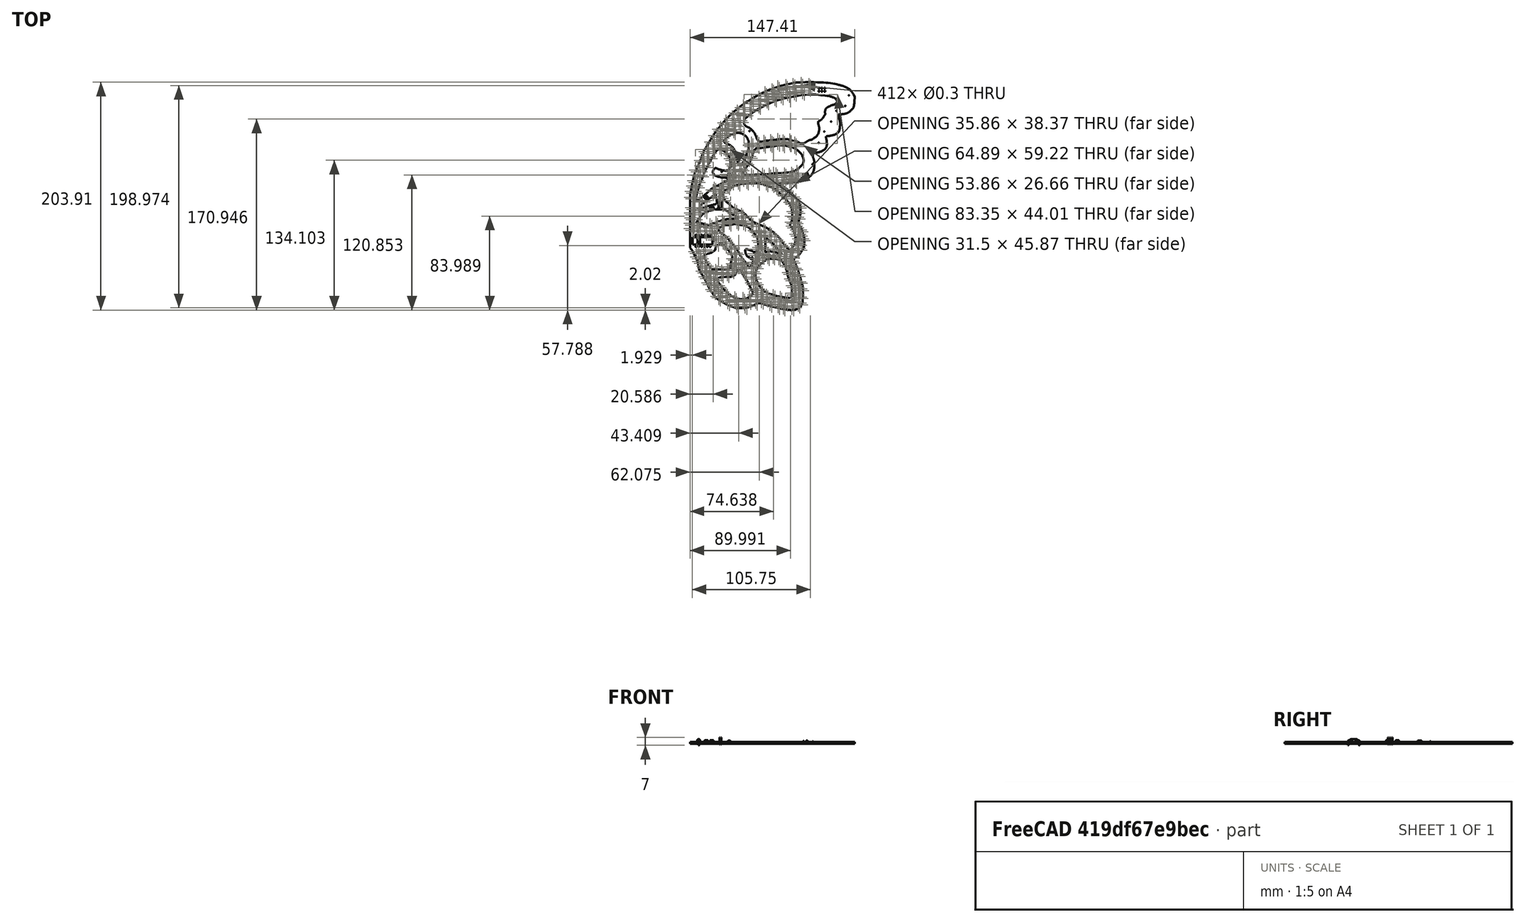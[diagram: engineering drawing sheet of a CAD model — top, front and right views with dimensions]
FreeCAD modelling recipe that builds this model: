
FCSTD DOCUMENT  (FreeCAD 0.21R30454 (Git))
Label: StarboardWing
License: All rights reserved
LicenseURL: http://en.wikipedia.org/wiki/All_rights_reserved
objects: App::Link×254, Part::Feature×9, App::Part×4, PartDesign::CoordinateSystem×1
note: 10 computed .brp shape members not serialized (recipe doc carries the construction recipe); baked Part::Feature solids carry a one-line shape summary decoded from their .brp

FEATURE [PartDesign::CoordinateSystem] Local_CS_1785
  AttacherType = Attacher::AttachEngine3D
  MapMode = 2
  Support = -> [X_Axis001]
FEATURE [Part::Feature] Pcb_1785
  shape: bbox 147.4 x 203.9 x 1.6 mm, 4422 faces (baked)
FEATURE [App::Part] Board_Geoms_1785
  Group = -> [Pcb_1785]
  Origin = -> Origin
FEATURE [Part::Feature] Shape  label="D136_LED_RGB_1210_62a520bec992"
  Placement = pos=(204.1,-82.7,0) rot=(0,0,1;0rad)
  shape: bbox 3.2 x 2.7 x 1.11 mm, 98 faces (baked)
FEATURE [App::Link] D136_LED_RGB_1210_62a520bec992_ln_  label="D150_LED_RGB_1210_12039ab7eeb1"
  LinkPlacement = pos=(181.3,-75,0) rot=(0,0,1;0rad)
  LinkedObject = -> Shape
  Placement = pos=(181.3,-75,0) rot=(0,0,1;0rad)
FEATURE [App::Link] D136_LED_RGB_1210_62a520bec992_ln_001  label="D23_LED_RGB_1210_ea9085552632"
  LinkPlacement = pos=(183.359,-164.826,0) rot=(0,0,1;0rad)
  LinkedObject = -> Shape
  Placement = pos=(183.359,-164.826,0) rot=(0,0,1;0rad)
FEATURE [App::Link] D136_LED_RGB_1210_62a520bec992_ln_002  label="D9_LED_RGB_1210_9001bbad8535"
  LinkPlacement = pos=(187.8,-129.2,0) rot=(0,0,1;0rad)
  LinkedObject = -> Shape
  Placement = pos=(187.8,-129.2,0) rot=(0,0,1;0rad)
FEATURE [App::Link] D136_LED_RGB_1210_62a520bec992_ln_003  label="D134_LED_RGB_1210_4c37d6cb8a8d"
  LinkPlacement = pos=(215.859,-120.026,0) rot=(0,0,1;0rad)
  LinkedObject = -> Shape
  Placement = pos=(215.859,-120.026,0) rot=(0,0,1;0rad)
FEATURE [App::Link] D136_LED_RGB_1210_62a520bec992_ln_004  label="D81_LED_RGB_1210_f8f1b236e2ee"
  LinkPlacement = pos=(224.9,-174.7,0) rot=(0,0,1;0rad)
  LinkedObject = -> Shape
  Placement = pos=(224.9,-174.7,0) rot=(0,0,1;0rad)
FEATURE [App::Link] D136_LED_RGB_1210_62a520bec992_ln_005  label="D7_LED_RGB_1210_8e7839006ea9"
  LinkPlacement = pos=(176.2,-132.6,0) rot=(0,0,1;0rad)
  LinkedObject = -> Shape
  Placement = pos=(176.2,-132.6,0) rot=(0,0,1;0rad)
FEATURE [App::Link] D136_LED_RGB_1210_62a520bec992_ln_006  label="D193_LED_RGB_1210_c832a5a088d9"
  LinkPlacement = pos=(307.759,-11.8264,0) rot=(0,0,1;0rad)
  LinkedObject = -> Shape
  Placement = pos=(307.759,-11.8264,0) rot=(0,0,1;0rad)
FEATURE [App::Link] D136_LED_RGB_1210_62a520bec992_ln_007  label="D158_LED_RGB_1210_09a3a09bfe6b"
  LinkPlacement = pos=(196.1,-51.9,0) rot=(0,0,1;0rad)
  LinkedObject = -> Shape
  Placement = pos=(196.1,-51.9,0) rot=(0,0,1;0rad)
FEATURE [App::Link] D136_LED_RGB_1210_62a520bec992_ln_008  label="D114_LED_RGB_1210_9c8997dbba9e"
  LinkPlacement = pos=(260.5,-102.9,0) rot=(0,0,1;0rad)
  LinkedObject = -> Shape
  Placement = pos=(260.5,-102.9,0) rot=(0,0,1;0rad)
FEATURE [App::Link] D136_LED_RGB_1210_62a520bec992_ln_009  label="D36_LED_RGB_1210_b757f64c7942"
  LinkPlacement = pos=(201.959,-191.026,0) rot=(0,0,1;0rad)
  LinkedObject = -> Shape
  Placement = pos=(201.959,-191.026,0) rot=(0,0,1;0rad)
FEATURE [App::Link] D136_LED_RGB_1210_62a520bec992_ln_010  label="D218_LED_RGB_1210_dde6179954a0"
  LinkPlacement = pos=(276.2,-62.7,0) rot=(0,0,1;0rad)
  LinkedObject = -> Shape
  Placement = pos=(276.2,-62.7,0) rot=(0,0,1;0rad)
FEATURE [App::Link] D136_LED_RGB_1210_62a520bec992_ln_011  label="D55_LED_RGB_1210_d54d391acb56"
  LinkPlacement = pos=(261.1,-194.9,0) rot=(0,0,1;0rad)
  LinkedObject = -> Shape
  Placement = pos=(261.1,-194.9,0) rot=(0,0,1;0rad)
FEATURE [App::Link] D136_LED_RGB_1210_62a520bec992_ln_012  label="D141_LED_RGB_1210_632e38c38ab6"
  LinkPlacement = pos=(208.9,-73.4,0) rot=(0,0,1;0rad)
  LinkedObject = -> Shape
  Placement = pos=(208.9,-73.4,0) rot=(0,0,1;0rad)
FEATURE [App::Link] D136_LED_RGB_1210_62a520bec992_ln_013  label="D222_LED_RGB_1210_c6c191f252d3"
  LinkPlacement = pos=(259.159,-53.4264,0) rot=(0,0,1;0rad)
  LinkedObject = -> Shape
  Placement = pos=(259.159,-53.4264,0) rot=(0,0,1;0rad)
FEATURE [App::Link] D136_LED_RGB_1210_62a520bec992_ln_014  label="D146_LED_RGB_1210_0157bd98a823"
  LinkPlacement = pos=(190.5,-58.9,0) rot=(0,0,1;0rad)
  LinkedObject = -> Shape
  Placement = pos=(190.5,-58.9,0) rot=(0,0,1;0rad)
FEATURE [App::Link] D136_LED_RGB_1210_62a520bec992_ln_015  label="D186_LED_RGB_1210_e3d56bbb0ae5"
  LinkPlacement = pos=(270.65,-7.45,0) rot=(0,0,1;0rad)
  LinkedObject = -> Shape
  Placement = pos=(270.65,-7.45,0) rot=(0,0,1;0rad)
FEATURE [App::Link] D136_LED_RGB_1210_62a520bec992_ln_016  label="D164_LED_RGB_1210_3ddcdd4b0932"
  LinkPlacement = pos=(209.2,-38.3,0) rot=(0,0,1;0rad)
  LinkedObject = -> Shape
  Placement = pos=(209.2,-38.3,0) rot=(0,0,1;0rad)
FEATURE [App::Link] D136_LED_RGB_1210_62a520bec992_ln_017  label="D64_LED_RGB_1210_adbd692ccdd2"
  LinkPlacement = pos=(259.759,-170.426,0) rot=(0,0,1;0rad)
  LinkedObject = -> Shape
  Placement = pos=(259.759,-170.426,0) rot=(0,0,1;0rad)
FEATURE [Part::Feature] Shape001  label="U4_SOT_23_5_fc069c77c7b4"
  Placement = pos=(183.6,-102.5,0) rot=(0,0,1;0.785398rad)
  shape: bbox 3.677 x 3.677 x 1.55 mm, 109 faces (baked)
FEATURE [App::Link] D136_LED_RGB_1210_62a520bec992_ln_018  label="D206_LED_RGB_1210_81ef24c7bf4b"
  LinkPlacement = pos=(298.859,-42.9264,0) rot=(0,0,1;0rad)
  LinkedObject = -> Shape
  Placement = pos=(298.859,-42.9264,0) rot=(0,0,1;0rad)
FEATURE [App::Link] D136_LED_RGB_1210_62a520bec992_ln_019  label="D15_LED_RGB_1210_b64d4fa2ef47"
  LinkPlacement = pos=(209.5,-152.9,0) rot=(0,0,1;0rad)
  LinkedObject = -> Shape
  Placement = pos=(209.5,-152.9,0) rot=(0,0,1;0rad)
FEATURE [App::Link] D136_LED_RGB_1210_62a520bec992_ln_020  label="D31_LED_RGB_1210_d7673fbed014"
  LinkPlacement = pos=(187.6,-179.8,0) rot=(0,0,1;0rad)
  LinkedObject = -> Shape
  Placement = pos=(187.6,-179.8,0) rot=(0,0,1;0rad)
FEATURE [App::Link] D136_LED_RGB_1210_62a520bec992_ln_021  label="D167_LED_RGB_1210_684f7f202117"
  LinkPlacement = pos=(213.559,-34.7264,0) rot=(0,0,1;0rad)
  LinkedObject = -> Shape
  Placement = pos=(213.559,-34.7264,0) rot=(0,0,1;0rad)
FEATURE [App::Link] D136_LED_RGB_1210_62a520bec992_ln_022  label="D210_LED_RGB_1210_f6960930e73a"
  LinkPlacement = pos=(286.659,-45.4264,0) rot=(0,0,1;0rad)
  LinkedObject = -> Shape
  Placement = pos=(286.659,-45.4264,0) rot=(0,0,1;0rad)
FEATURE [App::Link] D136_LED_RGB_1210_62a520bec992_ln_023  label="D50_LED_RGB_1210_4bd25c12756e"
  LinkPlacement = pos=(248.5,-199,0) rot=(0,0,1;0rad)
  LinkedObject = -> Shape
  Placement = pos=(248.5,-199,0) rot=(0,0,1;0rad)
FEATURE [App::Link] D136_LED_RGB_1210_62a520bec992_ln_024  label="D58_LED_RGB_1210_764fe6c10639"
  LinkPlacement = pos=(263.559,-188.926,0) rot=(0,0,1;0rad)
  LinkedObject = -> Shape
  Placement = pos=(263.559,-188.926,0) rot=(0,0,1;0rad)
FEATURE [App::Link] D136_LED_RGB_1210_62a520bec992_ln_025  label="D51_LED_RGB_1210_a85785bf3345"
  LinkPlacement = pos=(250.4,-194.3,0) rot=(0,0,1;0rad)
  LinkedObject = -> Shape
  Placement = pos=(250.4,-194.3,0) rot=(0,0,1;0rad)
FEATURE [App::Link] D136_LED_RGB_1210_62a520bec992_ln_026  label="D67_LED_RGB_1210_223aec051fc1"
  LinkPlacement = pos=(259.6,-160.4,0) rot=(0,0,1;0rad)
  LinkedObject = -> Shape
  Placement = pos=(259.6,-160.4,0) rot=(0,0,1;0rad)
FEATURE [App::Link] D136_LED_RGB_1210_62a520bec992_ln_027  label="D71_LED_RGB_1210_47d4682ee98f"
  LinkPlacement = pos=(249.2,-156.15,0) rot=(0,0,1;0rad)
  LinkedObject = -> Shape
  Placement = pos=(249.2,-156.15,0) rot=(0,0,1;0rad)
FEATURE [App::Link] U4_SOT_23_5_fc069c77c7b4_ln_  label="U3_SOT_23_5_68d5d64a2f14"
  LinkPlacement = pos=(172.5,-107.4,0) rot=(0,0,1;0rad)
  LinkedObject = -> Shape001
  Placement = pos=(172.5,-107.4,0) rot=(0,0,1;0rad)
FEATURE [App::Link] D136_LED_RGB_1210_62a520bec992_ln_028  label="D165_LED_RGB_1210_a3eefff06263"
  LinkPlacement = pos=(202,-36.65,0) rot=(0,0,1;0rad)
  LinkedObject = -> Shape
  Placement = pos=(202,-36.65,0) rot=(0,0,1;0rad)
FEATURE [App::Link] D136_LED_RGB_1210_62a520bec992_ln_029  label="D84_LED_RGB_1210_c73b158b3e06"
  LinkPlacement = pos=(219.05,-169.75,0) rot=(0,0,1;0rad)
  LinkedObject = -> Shape
  Placement = pos=(219.05,-169.75,0) rot=(0,0,1;0rad)
FEATURE [App::Link] D136_LED_RGB_1210_62a520bec992_ln_030  label="D101_LED_RGB_1210_1ee6ac56c98f"
  LinkPlacement = pos=(254.1,-150.4,0) rot=(0,0,1;0rad)
  LinkedObject = -> Shape
  Placement = pos=(254.1,-150.4,0) rot=(0,0,1;0rad)
FEATURE [Part::Feature] Shape002  label="C2_C_1206_3216Metric_b79cb4619a35"
  Placement = pos=(188.4,-111.5,0) rot=(0,0,1;3.14159rad)
  shape: bbox 3.2 x 1.6 x 1.6 mm, 28 faces (baked)
FEATURE [App::Link] D136_LED_RGB_1210_62a520bec992_ln_031  label="D52_LED_RGB_1210_378109606834"
  LinkPlacement = pos=(253.35,-200.45,0) rot=(0,0,1;0rad)
  LinkedObject = -> Shape
  Placement = pos=(253.35,-200.45,0) rot=(0,0,1;0rad)
FEATURE [App::Link] D136_LED_RGB_1210_62a520bec992_ln_032  label="D46_LED_RGB_1210_a2881a9ad48e"
  LinkPlacement = pos=(233.8,-194.5,0) rot=(0,0,1;0rad)
  LinkedObject = -> Shape
  Placement = pos=(233.8,-194.5,0) rot=(0,0,1;0rad)
FEATURE [App::Link] D136_LED_RGB_1210_62a520bec992_ln_033  label="D180_LED_RGB_1210_3362baaad274"
  LinkPlacement = pos=(251.6,-11.45,0) rot=(0,0,1;0rad)
  LinkedObject = -> Shape
  Placement = pos=(251.6,-11.45,0) rot=(0,0,1;0rad)
FEATURE [App::Link] D136_LED_RGB_1210_62a520bec992_ln_034  label="D247_LED_RGB_1210_6b35466e723f"
  LinkPlacement = pos=(265.5,-81.6,0) rot=(0,0,1;0rad)
  LinkedObject = -> Shape
  Placement = pos=(265.5,-81.6,0) rot=(0,0,1;0rad)
FEATURE [App::Link] D136_LED_RGB_1210_62a520bec992_ln_035  label="D100_LED_RGB_1210_c7f5be310b96"
  LinkPlacement = pos=(250.159,-146.226,0) rot=(0,0,1;0rad)
  LinkedObject = -> Shape
  Placement = pos=(250.159,-146.226,0) rot=(0,0,1;0rad)
FEATURE [App::Link] D136_LED_RGB_1210_62a520bec992_ln_036  label="D60_LED_RGB_1210_50de1819820a"
  LinkPlacement = pos=(263.259,-182.326,0) rot=(0,0,1;0rad)
  LinkedObject = -> Shape
  Placement = pos=(263.259,-182.326,0) rot=(0,0,1;0rad)
FEATURE [App::Link] D136_LED_RGB_1210_62a520bec992_ln_037  label="D12_LED_RGB_1210_b87074a79a7a"
  LinkPlacement = pos=(197.65,-138.25,0) rot=(0,0,1;0rad)
  LinkedObject = -> Shape
  Placement = pos=(197.65,-138.25,0) rot=(0,0,1;0rad)
FEATURE [App::Link] D136_LED_RGB_1210_62a520bec992_ln_038  label="D109_LED_RGB_1210_2ca5b701bd8b"
  LinkPlacement = pos=(262.4,-125.3,0) rot=(0,0,1;0rad)
  LinkedObject = -> Shape
  Placement = pos=(262.4,-125.3,0) rot=(0,0,1;0rad)
FEATURE [App::Link] D136_LED_RGB_1210_62a520bec992_ln_039  label="D223_LED_RGB_1210_cb616f081e86"
  LinkPlacement = pos=(253,-54.2,0) rot=(0,0,1;0rad)
  LinkedObject = -> Shape
  Placement = pos=(253,-54.2,0) rot=(0,0,1;0rad)
FEATURE [App::Link] D136_LED_RGB_1210_62a520bec992_ln_040  label="D221_LED_RGB_1210_1da33f8036cf"
  LinkPlacement = pos=(263.559,-56.3264,0) rot=(0,0,1;0rad)
  LinkedObject = -> Shape
  Placement = pos=(263.559,-56.3264,0) rot=(0,0,1;0rad)
FEATURE [App::Link] D136_LED_RGB_1210_62a520bec992_ln_041  label="D189_LED_RGB_1210_f086901acdd8"
  LinkPlacement = pos=(300.6,-5.1,0) rot=(0,0,1;0rad)
  LinkedObject = -> Shape
  Placement = pos=(300.6,-5.1,0) rot=(0,0,1;0rad)
FEATURE [App::Link] D136_LED_RGB_1210_62a520bec992_ln_042  label="D94_LED_RGB_1210_8ded45fa4095"
  LinkPlacement = pos=(232.359,-137.326,0) rot=(0,0,1;0rad)
  LinkedObject = -> Shape
  Placement = pos=(232.359,-137.326,0) rot=(0,0,1;0rad)
FEATURE [App::Link] D136_LED_RGB_1210_62a520bec992_ln_043  label="D57_LED_RGB_1210_6bb447222a72"
  LinkPlacement = pos=(266.859,-192.326,0) rot=(0,0,1;0rad)
  LinkedObject = -> Shape
  Placement = pos=(266.859,-192.326,0) rot=(0,0,1;0rad)
FEATURE [App::Link] D136_LED_RGB_1210_62a520bec992_ln_044  label="D156_LED_RGB_1210_adc01ad6926a"
  LinkPlacement = pos=(172,-103.05,0) rot=(0,0,1;0rad)
  LinkedObject = -> Shape
  Placement = pos=(172,-103.05,0) rot=(0,0,1;0rad)
FEATURE [App::Link] D136_LED_RGB_1210_62a520bec992_ln_045  label="D11_LED_RGB_1210_ba18253b5278"
  LinkPlacement = pos=(192,-139.8,0) rot=(0,0,1;0rad)
  LinkedObject = -> Shape
  Placement = pos=(192,-139.8,0) rot=(0,0,1;0rad)
FEATURE [App::Link] D136_LED_RGB_1210_62a520bec992_ln_046  label="D62_LED_RGB_1210_91df49d3e2f4"
  LinkPlacement = pos=(261.6,-176.3,0) rot=(0,0,1;0rad)
  LinkedObject = -> Shape
  Placement = pos=(261.6,-176.3,0) rot=(0,0,1;0rad)
FEATURE [App::Link] D136_LED_RGB_1210_62a520bec992_ln_047  label="D216_LED_RGB_1210_a3b31d0b2d53"
  LinkPlacement = pos=(275.7,-54.9,0) rot=(0,0,1;0rad)
  LinkedObject = -> Shape
  Placement = pos=(275.7,-54.9,0) rot=(0,0,1;0rad)
FEATURE [App::Link] D136_LED_RGB_1210_62a520bec992_ln_048  label="D229_LED_RGB_1210_5107d2615a96"
  LinkPlacement = pos=(224.7,-47.1,0) rot=(0,0,1;0rad)
  LinkedObject = -> Shape
  Placement = pos=(224.7,-47.1,0) rot=(0,0,1;0rad)
FEATURE [App::Link] D136_LED_RGB_1210_62a520bec992_ln_049  label="D191_LED_RGB_1210_c8a7f353cc4c"
  LinkPlacement = pos=(302.7,-10.3,0) rot=(0,0,1;0rad)
  LinkedObject = -> Shape
  Placement = pos=(302.7,-10.3,0) rot=(0,0,1;0rad)
FEATURE [App::Link] D136_LED_RGB_1210_62a520bec992_ln_050  label="D215_LED_RGB_1210_5ee730b57f91"
  LinkPlacement = pos=(284.959,-57.4264,0) rot=(0,0,1;0rad)
  LinkedObject = -> Shape
  Placement = pos=(284.959,-57.4264,0) rot=(0,0,1;0rad)
FEATURE [App::Link] D136_LED_RGB_1210_62a520bec992_ln_051  label="D106_LED_RGB_1210_3480d8f7ef54"
  LinkPlacement = pos=(266.359,-136.326,0) rot=(0,0,1;0rad)
  LinkedObject = -> Shape
  Placement = pos=(266.359,-136.326,0) rot=(0,0,1;0rad)
FEATURE [App::Link] D136_LED_RGB_1210_62a520bec992_ln_052  label="D122_LED_RGB_1210_edae958e6801"
  LinkPlacement = pos=(212.9,-88.5,0) rot=(0,0,1;0rad)
  LinkedObject = -> Shape
  Placement = pos=(212.9,-88.5,0) rot=(0,0,1;0rad)
FEATURE [App::Link] D136_LED_RGB_1210_62a520bec992_ln_053  label="D184_LED_RGB_1210_6b556ea57100"
  LinkPlacement = pos=(262.1,-3.7,0) rot=(0,0,1;0rad)
  LinkedObject = -> Shape
  Placement = pos=(262.1,-3.7,0) rot=(0,0,1;0rad)
FEATURE [App::Link] D136_LED_RGB_1210_62a520bec992_ln_054  label="D172_LED_RGB_1210_7e16bd91dec5"
  LinkPlacement = pos=(224.9,-17.8,0) rot=(0,0,1;0rad)
  LinkedObject = -> Shape
  Placement = pos=(224.9,-17.8,0) rot=(0,0,1;0rad)
FEATURE [App::Link] D136_LED_RGB_1210_62a520bec992_ln_056  label="D231_LED_RGB_1210_1870ebb3e0c7"
  LinkPlacement = pos=(215.559,-40.8264,0) rot=(0,0,1;0rad)
  LinkedObject = -> Shape
  Placement = pos=(215.559,-40.8264,0) rot=(0,0,1;0rad)
FEATURE [App::Link] D136_LED_RGB_1210_62a520bec992_ln_057  label="D22_LED_RGB_1210_787f26744da4"
  LinkPlacement = pos=(187.159,-168.926,0) rot=(0,0,1;0rad)
  LinkedObject = -> Shape
  Placement = pos=(187.159,-168.926,0) rot=(0,0,1;0rad)
FEATURE [App::Link] D136_LED_RGB_1210_62a520bec992_ln_058  label="D155_LED_RGB_1210_d8a960a572d5"
  LinkPlacement = pos=(172.659,-97.9264,0) rot=(0,0,1;0rad)
  LinkedObject = -> Shape
  Placement = pos=(172.659,-97.9264,0) rot=(0,0,1;0rad)
FEATURE [App::Link] D136_LED_RGB_1210_62a520bec992_ln_059  label="D129_LED_RGB_1210_9cf1fb1399dd"
  LinkPlacement = pos=(179,-106.4,0) rot=(0,0,1;0.785398rad)
  LinkedObject = -> Shape
  Placement = pos=(179,-106.4,0) rot=(0,0,1;0.785398rad)
FEATURE [App::Link] D136_LED_RGB_1210_62a520bec992_ln_060  label="D32_LED_RGB_1210_9dc2df0a11e0"
  LinkPlacement = pos=(193.55,-182.35,0) rot=(0,0,1;0rad)
  LinkedObject = -> Shape
  Placement = pos=(193.55,-182.35,0) rot=(0,0,1;0rad)
FEATURE [App::Link] D136_LED_RGB_1210_62a520bec992_ln_061  label="D79_LED_RGB_1210_894db1ea51ae"
  LinkPlacement = pos=(226.75,-165.55,0) rot=(0,0,1;0rad)
  LinkedObject = -> Shape
  Placement = pos=(226.75,-165.55,0) rot=(0,0,1;0rad)
FEATURE [App::Link] D136_LED_RGB_1210_62a520bec992_ln_062  label="D144_LED_RGB_1210_453888b4b232"
  LinkPlacement = pos=(201.959,-59.4264,0) rot=(0,0,1;0rad)
  LinkedObject = -> Shape
  Placement = pos=(201.959,-59.4264,0) rot=(0,0,1;0rad)
FEATURE [App::Link] D136_LED_RGB_1210_62a520bec992_ln_063  label="D34_LED_RGB_1210_d52e7bb4ad5a"
  LinkPlacement = pos=(197.4,-187.6,0) rot=(0,0,1;0rad)
  LinkedObject = -> Shape
  Placement = pos=(197.4,-187.6,0) rot=(0,0,1;0rad)
FEATURE [App::Link] D136_LED_RGB_1210_62a520bec992_ln_064  label="D29_LED_RGB_1210_4de864dce945"
  LinkPlacement = pos=(185.15,-174.25,0) rot=(0,0,1;0rad)
  LinkedObject = -> Shape
  Placement = pos=(185.15,-174.25,0) rot=(0,0,1;0rad)
FEATURE [App::Link] D136_LED_RGB_1210_62a520bec992_ln_065  label="D113_LED_RGB_1210_828d5db3c49d"
  LinkPlacement = pos=(261.159,-107.626,0) rot=(0,0,1;0rad)
  LinkedObject = -> Shape
  Placement = pos=(261.159,-107.626,0) rot=(0,0,1;0rad)
FEATURE [App::Link] D136_LED_RGB_1210_62a520bec992_ln_066  label="D47_LED_RGB_1210_2027f9b859df"
  LinkPlacement = pos=(238.2,-192.35,0) rot=(0,0,1;0rad)
  LinkedObject = -> Shape
  Placement = pos=(238.2,-192.35,0) rot=(0,0,1;0rad)
FEATURE [App::Link] D136_LED_RGB_1210_62a520bec992_ln_067  label="D213_LED_RGB_1210_bec9f1c11f37"
  LinkPlacement = pos=(288.759,-54.5264,0) rot=(0,0,1;0rad)
  LinkedObject = -> Shape
  Placement = pos=(288.759,-54.5264,0) rot=(0,0,1;0rad)
FEATURE [App::Link] D136_LED_RGB_1210_62a520bec992_ln_068  label="D85_LED_RGB_1210_5bf5fdf50969"
  LinkPlacement = pos=(217.1,-165.6,0) rot=(0,0,1;0rad)
  LinkedObject = -> Shape
  Placement = pos=(217.1,-165.6,0) rot=(0,0,1;0rad)
FEATURE [App::Link] D136_LED_RGB_1210_62a520bec992_ln_069  label="D8_LED_RGB_1210_bd24e93f7dc5"
  LinkPlacement = pos=(183.059,-132.626,0) rot=(0,0,1;0rad)
  LinkedObject = -> Shape
  Placement = pos=(183.059,-132.626,0) rot=(0,0,1;0rad)
FEATURE [App::Link] D136_LED_RGB_1210_62a520bec992_ln_070  label="D219_LED_RGB_1210_7ca36ad61957"
  LinkPlacement = pos=(270.6,-60.4,0) rot=(0,0,1;0rad)
  LinkedObject = -> Shape
  Placement = pos=(270.6,-60.4,0) rot=(0,0,1;0rad)
FEATURE [App::Link] D136_LED_RGB_1210_62a520bec992_ln_071  label="D194_LED_RGB_1210_a02c116111b0"
  LinkPlacement = pos=(311.3,-16.8,0) rot=(0,0,1;0rad)
  LinkedObject = -> Shape
  Placement = pos=(311.3,-16.8,0) rot=(0,0,1;0rad)
FEATURE [App::Link] D136_LED_RGB_1210_62a520bec992_ln_072  label="D107_LED_RGB_1210_0a0746ffa430"
  LinkPlacement = pos=(266.9,-132.5,0) rot=(0,0,1;0rad)
  LinkedObject = -> Shape
  Placement = pos=(266.9,-132.5,0) rot=(0,0,1;0rad)
FEATURE [App::Link] D136_LED_RGB_1210_62a520bec992_ln_073  label="D145_LED_RGB_1210_f5378009967f"
  LinkPlacement = pos=(196.6,-57.1,0) rot=(0,0,1;0rad)
  LinkedObject = -> Shape
  Placement = pos=(196.6,-57.1,0) rot=(0,0,1;0rad)
FEATURE [App::Link] D136_LED_RGB_1210_62a520bec992_ln_074  label="D18_LED_RGB_1210_fc494d825121"
  LinkPlacement = pos=(207.7,-167.2,0) rot=(0,0,1;0rad)
  LinkedObject = -> Shape
  Placement = pos=(207.7,-167.2,0) rot=(0,0,1;0rad)
FEATURE [App::Link] D136_LED_RGB_1210_62a520bec992_ln_075  label="D133_LED_RGB_1210_a365262d003e"
  LinkPlacement = pos=(209.959,-116.126,0) rot=(0,0,1;0rad)
  LinkedObject = -> Shape
  Placement = pos=(209.959,-116.126,0) rot=(0,0,1;0rad)
FEATURE [App::Link] D136_LED_RGB_1210_62a520bec992_ln_076  label="D120_LED_RGB_1210_1de8b38d268b"
  LinkPlacement = pos=(220.559,-87.8264,0) rot=(0,0,1;0rad)
  LinkedObject = -> Shape
  Placement = pos=(220.559,-87.8264,0) rot=(0,0,1;0rad)
FEATURE [App::Link] D136_LED_RGB_1210_62a520bec992_ln_077  label="D187_LED_RGB_1210_8412c23d868f"
  LinkPlacement = pos=(276.159,-3.72639,0) rot=(0,0,1;0rad)
  LinkedObject = -> Shape
  Placement = pos=(276.159,-3.72639,0) rot=(0,0,1;0rad)
FEATURE [App::Link] D136_LED_RGB_1210_62a520bec992_ln_078  label="D41_LED_RGB_1210_7670d9bbceb9"
  LinkPlacement = pos=(219.2,-199.2,0) rot=(0,0,1;0rad)
  LinkedObject = -> Shape
  Placement = pos=(219.2,-199.2,0) rot=(0,0,1;0rad)
FEATURE [App::Link] D136_LED_RGB_1210_62a520bec992_ln_079  label="D35_LED_RGB_1210_252c8013e403"
  LinkPlacement = pos=(195.559,-191.626,0) rot=(0,0,1;0rad)
  LinkedObject = -> Shape
  Placement = pos=(195.559,-191.626,0) rot=(0,0,1;0rad)
FEATURE [App::Link] D136_LED_RGB_1210_62a520bec992_ln_081  label="D196_LED_RGB_1210_b728bd658690"
  LinkPlacement = pos=(311.959,-21.4264,0) rot=(0,0,1;0rad)
  LinkedObject = -> Shape
  Placement = pos=(311.959,-21.4264,0) rot=(0,0,1;0rad)
FEATURE [App::Link] D136_LED_RGB_1210_62a520bec992_ln_082  label="D227_LED_RGB_1210_af0846aa31f9"
  LinkPlacement = pos=(230.259,-55.0264,0) rot=(0,0,1;0rad)
  LinkedObject = -> Shape
  Placement = pos=(230.259,-55.0264,0) rot=(0,0,1;0rad)
FEATURE [App::Link] D136_LED_RGB_1210_62a520bec992_ln_083  label="D232_LED_RGB_1210_fb8289a4a3aa"
  LinkPlacement = pos=(224.859,-56.3264,0) rot=(0,0,1;0rad)
  LinkedObject = -> Shape
  Placement = pos=(224.859,-56.3264,0) rot=(0,0,1;0rad)
FEATURE [App::Link] D136_LED_RGB_1210_62a520bec992_ln_084  label="D89_LED_RGB_1210_274bd17ad472"
  LinkPlacement = pos=(205,-124.5,0) rot=(0,0,1;0rad)
  LinkedObject = -> Shape
  Placement = pos=(205,-124.5,0) rot=(0,0,1;0rad)
FEATURE [App::Link] D136_LED_RGB_1210_62a520bec992_ln_085  label="D212_LED_RGB_1210_13e51074f58c"
  LinkPlacement = pos=(284.2,-50.1,0) rot=(0,0,1;0rad)
  LinkedObject = -> Shape
  Placement = pos=(284.2,-50.1,0) rot=(0,0,1;0rad)
FEATURE [App::Link] D136_LED_RGB_1210_62a520bec992_ln_086  label="D131_LED_RGB_1210_7cfefdc31ccb"
  LinkPlacement = pos=(183.35,-113.25,0) rot=(0,0,1;0rad)
  LinkedObject = -> Shape
  Placement = pos=(183.35,-113.25,0) rot=(0,0,1;0rad)
FEATURE [App::Link] D136_LED_RGB_1210_62a520bec992_ln_087  label="D68_LED_RGB_1210_3f09e83a6821"
  LinkPlacement = pos=(255.1,-158.5,0) rot=(0,0,1;0rad)
  LinkedObject = -> Shape
  Placement = pos=(255.1,-158.5,0) rot=(0,0,1;0rad)
FEATURE [App::Link] D136_LED_RGB_1210_62a520bec992_ln_088  label="D56_LED_RGB_1210_fd3cac2ae8d4"
  LinkPlacement = pos=(266.6,-197.75,0) rot=(0,0,1;0rad)
  LinkedObject = -> Shape
  Placement = pos=(266.6,-197.75,0) rot=(0,0,1;0rad)
FEATURE [App::Link] D136_LED_RGB_1210_62a520bec992_ln_089  label="D90_LED_RGB_1210_3af3f6667f3d"
  LinkPlacement = pos=(211.659,-123.926,0) rot=(0,0,1;0rad)
  LinkedObject = -> Shape
  Placement = pos=(211.659,-123.926,0) rot=(0,0,1;0rad)
FEATURE [App::Link] D136_LED_RGB_1210_62a520bec992_ln_090  label="D86_LED_RGB_1210_c2b8e460d749"
  LinkPlacement = pos=(215.3,-161.8,0) rot=(0,0,1;0rad)
  LinkedObject = -> Shape
  Placement = pos=(215.3,-161.8,0) rot=(0,0,1;0rad)
FEATURE [App::Link] C2_C_1206_3216Metric_b79cb4619a35_ln_  label="C44_C_1206_3216Metric_271b0f8e82f6"
  LinkPlacement = pos=(268.4,-85.5,0) rot=(0,0,1;0rad)
  LinkedObject = -> Shape002
  Placement = pos=(268.4,-85.5,0) rot=(0,0,1;0rad)
FEATURE [App::Link] D136_LED_RGB_1210_62a520bec992_ln_091  label="D198_LED_RGB_1210_a531206362b3"
  LinkPlacement = pos=(306.859,-25.2264,0) rot=(0,0,1;0rad)
  LinkedObject = -> Shape
  Placement = pos=(306.859,-25.2264,0) rot=(0,0,1;0rad)
FEATURE [Part::Feature] Shape003  label="C3_C_0603_1608Metric_700197c864c6"
  Placement = pos=(270.7,-82.2,0) rot=(0,0,1;1.5708rad)
  shape: bbox 0.8 x 1.6 x 0.8 mm, 28 faces (baked)
FEATURE [App::Link] D136_LED_RGB_1210_62a520bec992_ln_092  label="D75_LED_RGB_1210_d5f237ff8ab4"
  LinkPlacement = pos=(230.659,-157.726,0) rot=(0,0,1;0rad)
  LinkedObject = -> Shape
  Placement = pos=(230.659,-157.726,0) rot=(0,0,1;0rad)
FEATURE [App::Link] D136_LED_RGB_1210_62a520bec992_ln_093  label="D246_LED_RGB_1210_59c74dbcb773"
  LinkPlacement = pos=(273.959,-66.8264,0) rot=(0,0,1;0rad)
  LinkedObject = -> Shape
  Placement = pos=(273.959,-66.8264,0) rot=(0,0,1;0rad)
FEATURE [App::Link] C2_C_1206_3216Metric_b79cb4619a35_ln_001  label="C40_C_1206_3216Metric_c453f5429977"
  LinkPlacement = pos=(295.7,-4.8,0) rot=(0,0,1;1.5708rad)
  LinkedObject = -> Shape002
  Placement = pos=(295.7,-4.8,0) rot=(0,0,1;1.5708rad)
FEATURE [App::Link] D136_LED_RGB_1210_62a520bec992_ln_094  label="D13_LED_RGB_1210_12306b9c6f1e"
  LinkPlacement = pos=(201,-143.2,0) rot=(0,0,1;0rad)
  LinkedObject = -> Shape
  Placement = pos=(201,-143.2,0) rot=(0,0,1;0rad)
FEATURE [App::Link] D136_LED_RGB_1210_62a520bec992_ln_095  label="D78_LED_RGB_1210_ea5d2c3d57e0"
  LinkPlacement = pos=(227.9,-161.4,0) rot=(0,0,1;0rad)
  LinkedObject = -> Shape
  Placement = pos=(227.9,-161.4,0) rot=(0,0,1;0rad)
FEATURE [App::Link] D136_LED_RGB_1210_62a520bec992_ln_096  label="D3_LED_RGB_1210_c41b436d01a6"
  LinkPlacement = pos=(172.359,-121.626,0) rot=(0,0,1;0rad)
  LinkedObject = -> Shape
  Placement = pos=(172.359,-121.626,0) rot=(0,0,1;0rad)
FEATURE [App::Link] D136_LED_RGB_1210_62a520bec992_ln_097  label="D24_LED_RGB_1210_26dd01453c45"
  LinkPlacement = pos=(179.559,-160.726,0) rot=(0,0,1;0rad)
  LinkedObject = -> Shape
  Placement = pos=(179.559,-160.726,0) rot=(0,0,1;0rad)
FEATURE [App::Link] D136_LED_RGB_1210_62a520bec992_ln_098  label="D98_LED_RGB_1210_7ade84ffe8a4"
  LinkPlacement = pos=(241.3,-136.8,0) rot=(0,0,1;0rad)
  LinkedObject = -> Shape
  Placement = pos=(241.3,-136.8,0) rot=(0,0,1;0rad)
FEATURE [App::Link] D136_LED_RGB_1210_62a520bec992_ln_099  label="D96_LED_RGB_1210_be6911c69d5c"
  LinkPlacement = pos=(233,-148,0) rot=(0,0,1;0rad)
  LinkedObject = -> Shape
  Placement = pos=(233,-148,0) rot=(0,0,1;0rad)
FEATURE [App::Link] D136_LED_RGB_1210_62a520bec992_ln_100  label="D49_LED_RGB_1210_66b2c7e6ced7"
  LinkPlacement = pos=(241.45,-197.25,0) rot=(0,0,1;0rad)
  LinkedObject = -> Shape
  Placement = pos=(241.45,-197.25,0) rot=(0,0,1;0rad)
FEATURE [App::Link] D136_LED_RGB_1210_62a520bec992_ln_101  label="D143_LED_RGB_1210_243f32b69a39"
  LinkPlacement = pos=(205.959,-63.7264,0) rot=(0,0,1;0rad)
  LinkedObject = -> Shape
  Placement = pos=(205.959,-63.7264,0) rot=(0,0,1;0rad)
FEATURE [App::Link] D136_LED_RGB_1210_62a520bec992_ln_102  label="D138_LED_RGB_1210_53f483fe4a79"
  LinkPlacement = pos=(194.1,-80.5,0) rot=(0,0,1;0rad)
  LinkedObject = -> Shape
  Placement = pos=(194.1,-80.5,0) rot=(0,0,1;0rad)
FEATURE [App::Link] D136_LED_RGB_1210_62a520bec992_ln_103  label="D181_LED_RGB_1210_ce4a4e9c3fe1"
  LinkPlacement = pos=(255.55,-4.85,0) rot=(0,0,1;0rad)
  LinkedObject = -> Shape
  Placement = pos=(255.55,-4.85,0) rot=(0,0,1;0rad)
FEATURE [App::Link] D136_LED_RGB_1210_62a520bec992_ln_104  label="D178_LED_RGB_1210_9ffd6ba172f6"
  LinkPlacement = pos=(245.6,-13.5,0) rot=(0,0,1;0rad)
  LinkedObject = -> Shape
  Placement = pos=(245.6,-13.5,0) rot=(0,0,1;0rad)
FEATURE [App::Link] D136_LED_RGB_1210_62a520bec992_ln_105  label="D207_LED_RGB_1210_21ac523cdb0e"
  LinkPlacement = pos=(294.859,-38.9264,0) rot=(0,0,1;0rad)
  LinkedObject = -> Shape
  Placement = pos=(294.859,-38.9264,0) rot=(0,0,1;0rad)
FEATURE [App::Link] D136_LED_RGB_1210_62a520bec992_ln_106  label="D14_LED_RGB_1210_222e86e72b79"
  LinkPlacement = pos=(205.6,-146.7,0) rot=(0,0,1;0rad)
  LinkedObject = -> Shape
  Placement = pos=(205.6,-146.7,0) rot=(0,0,1;0rad)
FEATURE [App::Link] D136_LED_RGB_1210_62a520bec992_ln_107  label="D82_LED_RGB_1210_a9a8e1b79abb"
  LinkPlacement = pos=(226.75,-179.65,0) rot=(0,0,1;0rad)
  LinkedObject = -> Shape
  Placement = pos=(226.75,-179.65,0) rot=(0,0,1;0rad)
FEATURE [App::Link] D136_LED_RGB_1210_62a520bec992_ln_108  label="D175_LED_RGB_1210_0df9ab1ddb9f"
  LinkPlacement = pos=(236.8,-11.1,0) rot=(0,0,1;0rad)
  LinkedObject = -> Shape
  Placement = pos=(236.8,-11.1,0) rot=(0,0,1;0rad)
FEATURE [App::Link] D136_LED_RGB_1210_62a520bec992_ln_109  label="D44_LED_RGB_1210_4afc21a0c517"
  LinkPlacement = pos=(228.759,-190.626,0) rot=(0,0,1;0rad)
  LinkedObject = -> Shape
  Placement = pos=(228.759,-190.626,0) rot=(0,0,1;0rad)
FEATURE [App::Link] D136_LED_RGB_1210_62a520bec992_ln_110  label="D226_LED_RGB_1210_77ae9effce08"
  LinkPlacement = pos=(235.759,-54.7264,0) rot=(0,0,1;0rad)
  LinkedObject = -> Shape
  Placement = pos=(235.759,-54.7264,0) rot=(0,0,1;0rad)
FEATURE [App::Link] D136_LED_RGB_1210_62a520bec992_ln_111  label="D137_LED_RGB_1210_3c75f59faa47"
  LinkPlacement = pos=(199.059,-82.3264,0) rot=(0,0,1;0rad)
  LinkedObject = -> Shape
  Placement = pos=(199.059,-82.3264,0) rot=(0,0,1;0rad)
FEATURE [App::Link] D136_LED_RGB_1210_62a520bec992_ln_112  label="D21_LED_RGB_1210_33af59d753b4"
  LinkPlacement = pos=(192.759,-170.126,0) rot=(0,0,1;0rad)
  LinkedObject = -> Shape
  Placement = pos=(192.759,-170.126,0) rot=(0,0,1;0rad)
FEATURE [App::Link] D136_LED_RGB_1210_62a520bec992_ln_114  label="D123_LED_RGB_1210_d079ec9b3556"
  LinkPlacement = pos=(209.559,-84.2264,0) rot=(0,0,1;0rad)
  LinkedObject = -> Shape
  Placement = pos=(209.559,-84.2264,0) rot=(0,0,1;0rad)
FEATURE [App::Link] D136_LED_RGB_1210_62a520bec992_ln_115  label="D53_LED_RGB_1210_afa1ec7fb986"
  LinkPlacement = pos=(255.4,-196,0) rot=(0,0,1;0rad)
  LinkedObject = -> Shape
  Placement = pos=(255.4,-196,0) rot=(0,0,1;0rad)
FEATURE [App::Link] D136_LED_RGB_1210_62a520bec992_ln_116  label="D190_LED_RGB_1210_e2926fa54dfc"
  LinkPlacement = pos=(305.959,-6.82639,0) rot=(0,0,1;0rad)
  LinkedObject = -> Shape
  Placement = pos=(305.959,-6.82639,0) rot=(0,0,1;0rad)
FEATURE [App::Link] D136_LED_RGB_1210_62a520bec992_ln_117  label="D40_LED_RGB_1210_e51dabcca86d"
  LinkPlacement = pos=(217.2,-195.4,0) rot=(0,0,1;0rad)
  LinkedObject = -> Shape
  Placement = pos=(217.2,-195.4,0) rot=(0,0,1;0rad)
FEATURE [App::Link] D136_LED_RGB_1210_62a520bec992_ln_118  label="D121_LED_RGB_1210_bca63f975268"
  LinkPlacement = pos=(216.55,-84.35,0) rot=(0,0,1;0rad)
  LinkedObject = -> Shape
  Placement = pos=(216.55,-84.35,0) rot=(0,0,1;0rad)
FEATURE [App::Link] D136_LED_RGB_1210_62a520bec992_ln_119  label="D33_LED_RGB_1210_a20cd40f53f5"
  LinkPlacement = pos=(191.1,-185.8,0) rot=(0,0,1;0rad)
  LinkedObject = -> Shape
  Placement = pos=(191.1,-185.8,0) rot=(0,0,1;0rad)
FEATURE [App::Link] D136_LED_RGB_1210_62a520bec992_ln_120  label="D10_LED_RGB_1210_077b191f04b2"
  LinkPlacement = pos=(190,-134,0) rot=(0,0,1;0rad)
  LinkedObject = -> Shape
  Placement = pos=(190,-134,0) rot=(0,0,1;0rad)
FEATURE [App::Link] D136_LED_RGB_1210_62a520bec992_ln_121  label="D153_LED_RGB_1210_08de6983d4b1"
  LinkPlacement = pos=(174.859,-88.2264,0) rot=(0,0,1;0rad)
  LinkedObject = -> Shape
  Placement = pos=(174.859,-88.2264,0) rot=(0,0,1;0rad)
FEATURE [App::Link] D136_LED_RGB_1210_62a520bec992_ln_122  label="D182_LED_RGB_1210_17c916b7ca9c"
  LinkPlacement = pos=(257.3,-9.2,0) rot=(0,0,1;0rad)
  LinkedObject = -> Shape
  Placement = pos=(257.3,-9.2,0) rot=(0,0,1;0rad)
FEATURE [App::Link] D136_LED_RGB_1210_62a520bec992_ln_123  label="D54_LED_RGB_1210_efa55da82a0f"
  LinkPlacement = pos=(261.1,-200.5,0) rot=(0,0,1;0rad)
  LinkedObject = -> Shape
  Placement = pos=(261.1,-200.5,0) rot=(0,0,1;0rad)
FEATURE [App::Link] D136_LED_RGB_1210_62a520bec992_ln_124  label="D45_LED_RGB_1210_58b60f17caf7"
  LinkPlacement = pos=(233.35,-188.55,0) rot=(0,0,1;0rad)
  LinkedObject = -> Shape
  Placement = pos=(233.35,-188.55,0) rot=(0,0,1;0rad)
FEATURE [App::Link] D136_LED_RGB_1210_62a520bec992_ln_125  label="D197_LED_RGB_1210_70c94d4db8dc"
  LinkPlacement = pos=(303.359,-20.6264,0) rot=(0,0,1;0rad)
  LinkedObject = -> Shape
  Placement = pos=(303.359,-20.6264,0) rot=(0,0,1;0rad)
FEATURE [App::Link] D136_LED_RGB_1210_62a520bec992_ln_126  label="D2_LED_RGB_1210_4ffcff6675ae"
  LinkPlacement = pos=(173.1,-112.4,0) rot=(0,0,1;0rad)
  LinkedObject = -> Shape
  Placement = pos=(173.1,-112.4,0) rot=(0,0,1;0rad)
FEATURE [App::Link] D136_LED_RGB_1210_62a520bec992_ln_127  label="D88_LED_RGB_1210_3f14a4f6ae2b"
  LinkPlacement = pos=(198.859,-125.526,0) rot=(0,0,1;0rad)
  LinkedObject = -> Shape
  Placement = pos=(198.859,-125.526,0) rot=(0,0,1;0rad)
FEATURE [App::Link] D136_LED_RGB_1210_62a520bec992_ln_128  label="D162_LED_RGB_1210_75519ce188be"
  LinkPlacement = pos=(203.2,-41.6,0) rot=(0,0,1;0rad)
  LinkedObject = -> Shape
  Placement = pos=(203.2,-41.6,0) rot=(0,0,1;0rad)
FEATURE [Part::Feature] Shape004  label="U1_SOT_23_4b6a6773a716"
  Placement = pos=(273.7,-82.2,0) rot=(0,0,1;0rad)
  shape: bbox 2.5 x 3 x 1.2 mm, 76 faces (baked)
FEATURE [App::Link] D136_LED_RGB_1210_62a520bec992_ln_130  label="D176_LED_RGB_1210_48386e052522"
  LinkPlacement = pos=(238.8,-15.9,0) rot=(0,0,1;0rad)
  LinkedObject = -> Shape
  Placement = pos=(238.8,-15.9,0) rot=(0,0,1;0rad)
FEATURE [App::Link] D136_LED_RGB_1210_62a520bec992_ln_131  label="D72_LED_RGB_1210_74a8ea84f703"
  LinkPlacement = pos=(244.1,-154.8,0) rot=(0,0,1;0rad)
  LinkedObject = -> Shape
  Placement = pos=(244.1,-154.8,0) rot=(0,0,1;0rad)
FEATURE [App::Link] D136_LED_RGB_1210_62a520bec992_ln_132  label="D108_LED_RGB_1210_739de8030c63"
  LinkPlacement = pos=(263.2,-129,0) rot=(0,0,1;0rad)
  LinkedObject = -> Shape
  Placement = pos=(263.2,-129,0) rot=(0,0,1;0rad)
FEATURE [App::Link] D136_LED_RGB_1210_62a520bec992_ln_133  label="D103_LED_RGB_1210_896c93e42514"
  LinkPlacement = pos=(266.05,-149.05,0) rot=(0,0,1;0rad)
  LinkedObject = -> Shape
  Placement = pos=(266.05,-149.05,0) rot=(0,0,1;0rad)
FEATURE [App::Link] D136_LED_RGB_1210_62a520bec992_ln_134  label="D63_LED_RGB_1210_3dbb1e3be0e6"
  LinkPlacement = pos=(264.3,-172.4,0) rot=(0,0,1;0rad)
  LinkedObject = -> Shape
  Placement = pos=(264.3,-172.4,0) rot=(0,0,1;0rad)
FEATURE [App::Link] D136_LED_RGB_1210_62a520bec992_ln_135  label="D95_LED_RGB_1210_6d410ff1fabc"
  LinkPlacement = pos=(232.65,-142.05,0) rot=(0,0,1;0rad)
  LinkedObject = -> Shape
  Placement = pos=(232.65,-142.05,0) rot=(0,0,1;0rad)
FEATURE [App::Link] D136_LED_RGB_1210_62a520bec992_ln_136  label="D170_LED_RGB_1210_84f4caf03d5c"
  LinkPlacement = pos=(217.55,-22.95,0) rot=(0,0,1;0rad)
  LinkedObject = -> Shape
  Placement = pos=(217.55,-22.95,0) rot=(0,0,1;0rad)
FEATURE [App::Link] D136_LED_RGB_1210_62a520bec992_ln_137  label="D132_LED_RGB_1210_39e364661906"
  LinkPlacement = pos=(204.759,-113.126,0) rot=(0,0,1;0rad)
  LinkedObject = -> Shape
  Placement = pos=(204.759,-113.126,0) rot=(0,0,1;0rad)
FEATURE [App::Link] D136_LED_RGB_1210_62a520bec992_ln_138  label="D30_LED_RGB_1210_07571decdd41"
  LinkPlacement = pos=(190.8,-175.9,0) rot=(0,0,1;0rad)
  LinkedObject = -> Shape
  Placement = pos=(190.8,-175.9,0) rot=(0,0,1;0rad)
FEATURE [App::Link] D136_LED_RGB_1210_62a520bec992_ln_139  label="D16_LED_RGB_1210_9242cc2eed87"
  LinkPlacement = pos=(210,-158,0) rot=(0,0,1;0rad)
  LinkedObject = -> Shape
  Placement = pos=(210,-158,0) rot=(0,0,1;0rad)
FEATURE [App::Link] D136_LED_RGB_1210_62a520bec992_ln_140  label="D19_LED_RGB_1210_cb05497587f3"
  LinkPlacement = pos=(203.2,-170.4,0) rot=(0,0,1;0rad)
  LinkedObject = -> Shape
  Placement = pos=(203.2,-170.4,0) rot=(0,0,1;0rad)
FEATURE [App::Link] D136_LED_RGB_1210_62a520bec992_ln_141  label="D239_LED_RGB_1210_9c5008740159"
  LinkPlacement = pos=(243.4,-89.8,0) rot=(0,0,1;0rad)
  LinkedObject = -> Shape
  Placement = pos=(243.4,-89.8,0) rot=(0,0,1;0rad)
FEATURE [App::Link] C3_C_0603_1608Metric_700197c864c6_ln_  label="C42_C_0603_1608Metric_8efd535251a3"
  LinkPlacement = pos=(278.6,-8.4,0) rot=(0,0,1;3.14159rad)
  LinkedObject = -> Shape003
  Placement = pos=(278.6,-8.4,0) rot=(0,0,1;3.14159rad)
FEATURE [App::Link] D136_LED_RGB_1210_62a520bec992_ln_142  label="D105_LED_RGB_1210_2f7a4182f01c"
  LinkPlacement = pos=(268.959,-140.426,0) rot=(0,0,1;0rad)
  LinkedObject = -> Shape
  Placement = pos=(268.959,-140.426,0) rot=(0,0,1;0rad)
FEATURE [App::Link] D136_LED_RGB_1210_62a520bec992_ln_143  label="D111_LED_RGB_1210_fd07a01a22f6"
  LinkPlacement = pos=(263.9,-116,0) rot=(0,0,1;0rad)
  LinkedObject = -> Shape
  Placement = pos=(263.9,-116,0) rot=(0,0,1;0rad)
FEATURE [App::Link] D136_LED_RGB_1210_62a520bec992_ln_144  label="D149_LED_RGB_1210_914dd5457a6b"
  LinkPlacement = pos=(180.859,-70.0264,0) rot=(0,0,1;0rad)
  LinkedObject = -> Shape
  Placement = pos=(180.859,-70.0264,0) rot=(0,0,1;0rad)
FEATURE [App::Link] D136_LED_RGB_1210_62a520bec992_ln_145  label="D174_LED_RGB_1210_4063ea990139"
  LinkPlacement = pos=(231.55,-15.15,0) rot=(0,0,1;0rad)
  LinkedObject = -> Shape
  Placement = pos=(231.55,-15.15,0) rot=(0,0,1;0rad)
FEATURE [App::Link] C3_C_0603_1608Metric_700197c864c6_ln_001  label="C43_C_0603_1608Metric_3d8d81ffcbc8"
  LinkPlacement = pos=(278.6,-6.7,0) rot=(0,0,1;3.14159rad)
  LinkedObject = -> Shape003
  Placement = pos=(278.6,-6.7,0) rot=(0,0,1;3.14159rad)
FEATURE [App::Link] D136_LED_RGB_1210_62a520bec992_ln_146  label="D28_LED_RGB_1210_51e9a9c8c8db"
  LinkPlacement = pos=(182.759,-169.326,0) rot=(0,0,1;0rad)
  LinkedObject = -> Shape
  Placement = pos=(182.759,-169.326,0) rot=(0,0,1;0rad)
FEATURE [App::Link] D136_LED_RGB_1210_62a520bec992_ln_147  label="D42_LED_RGB_1210_9eaf27347b21"
  LinkPlacement = pos=(222.959,-194.726,0) rot=(0,0,1;0rad)
  LinkedObject = -> Shape
  Placement = pos=(222.959,-194.726,0) rot=(0,0,1;0rad)
FEATURE [App::Link] D136_LED_RGB_1210_62a520bec992_ln_148  label="D38_LED_RGB_1210_cc17a73a3e75"
  LinkPlacement = pos=(209.9,-194.7,0) rot=(0,0,1;0rad)
  LinkedObject = -> Shape
  Placement = pos=(209.9,-194.7,0) rot=(0,0,1;0rad)
FEATURE [App::Link] C2_C_1206_3216Metric_b79cb4619a35_ln_002  label="C39_C_1206_3216Metric_446bd29a878c"
  LinkPlacement = pos=(222.7,-21.3,0) rot=(0,0,1;0rad)
  LinkedObject = -> Shape002
  Placement = pos=(222.7,-21.3,0) rot=(0,0,1;0rad)
FEATURE [App::Link] D136_LED_RGB_1210_62a520bec992_ln_149  label="D48_LED_RGB_1210_36a0050f4f93"
  LinkPlacement = pos=(244.3,-192.6,0) rot=(0,0,1;0rad)
  LinkedObject = -> Shape
  Placement = pos=(244.3,-192.6,0) rot=(0,0,1;0rad)
FEATURE [App::Link] D136_LED_RGB_1210_62a520bec992_ln_150  label="D220_LED_RGB_1210_ade3fc4e9a5e"
  LinkPlacement = pos=(269.05,-56.75,0) rot=(0,0,1;0rad)
  LinkedObject = -> Shape
  Placement = pos=(269.05,-56.75,0) rot=(0,0,1;0rad)
FEATURE [App::Link] D136_LED_RGB_1210_62a520bec992_ln_151  label="D104_LED_RGB_1210_8572da40d27b"
  LinkPlacement = pos=(265.759,-144.526,0) rot=(0,0,1;0rad)
  LinkedObject = -> Shape
  Placement = pos=(265.759,-144.526,0) rot=(0,0,1;0rad)
FEATURE [App::Link] D136_LED_RGB_1210_62a520bec992_ln_152  label="D115_LED_RGB_1210_4928903ef0f2"
  LinkPlacement = pos=(254.85,-100.55,0) rot=(0,0,1;0rad)
  LinkedObject = -> Shape
  Placement = pos=(254.85,-100.55,0) rot=(0,0,1;0rad)
FEATURE [App::Link] D136_LED_RGB_1210_62a520bec992_ln_153  label="D214_LED_RGB_1210_643f84120ac4"
  LinkPlacement = pos=(280.6,-52.9,0) rot=(0,0,1;0rad)
  LinkedObject = -> Shape
  Placement = pos=(280.6,-52.9,0) rot=(0,0,1;0rad)
FEATURE [App::Link] D136_LED_RGB_1210_62a520bec992_ln_154  label="D87_LED_RGB_1210_21b08b48ec7a"
  LinkPlacement = pos=(193.059,-127.426,0) rot=(0,0,1;0rad)
  LinkedObject = -> Shape
  Placement = pos=(193.059,-127.426,0) rot=(0,0,1;0rad)
FEATURE [App::Link] D136_LED_RGB_1210_62a520bec992_ln_155  label="D93_LED_RGB_1210_0b370dfb5bac"
  LinkPlacement = pos=(229.359,-132.926,0) rot=(0,0,1;0rad)
  LinkedObject = -> Shape
  Placement = pos=(229.359,-132.926,0) rot=(0,0,1;0rad)
FEATURE [App::Link] D136_LED_RGB_1210_62a520bec992_ln_156  label="D154_LED_RGB_1210_94324b017783"
  LinkPlacement = pos=(174.059,-93.1264,0) rot=(0,0,1;0rad)
  LinkedObject = -> Shape
  Placement = pos=(174.059,-93.1264,0) rot=(0,0,1;0rad)
FEATURE [App::Link] D136_LED_RGB_1210_62a520bec992_ln_157  label="D147_LED_RGB_1210_964372ae1fe8"
  LinkPlacement = pos=(185.059,-62.2264,0) rot=(0,0,1;0rad)
  LinkedObject = -> Shape
  Placement = pos=(185.059,-62.2264,0) rot=(0,0,1;0rad)
FEATURE [App::Link] D136_LED_RGB_1210_62a520bec992_ln_158  label="D69_LED_RGB_1210_9cb8300ab2f2"
  LinkPlacement = pos=(259.25,-155.85,0) rot=(0,0,1;0rad)
  LinkedObject = -> Shape
  Placement = pos=(259.25,-155.85,0) rot=(0,0,1;0rad)
FEATURE [App::Link] D136_LED_RGB_1210_62a520bec992_ln_159  label="D39_LED_RGB_1210_4841d9836cfe"
  LinkPlacement = pos=(211.85,-199.15,0) rot=(0,0,1;0rad)
  LinkedObject = -> Shape
  Placement = pos=(211.85,-199.15,0) rot=(0,0,1;0rad)
FEATURE [App::Link] D136_LED_RGB_1210_62a520bec992_ln_160  label="D238_LED_RGB_1210_1f2b9df09682"
  LinkPlacement = pos=(240.7,-84.3,0) rot=(0,0,1;0rad)
  LinkedObject = -> Shape
  Placement = pos=(240.7,-84.3,0) rot=(0,0,1;0rad)
FEATURE [App::Link] D136_LED_RGB_1210_62a520bec992_ln_161  label="D117_LED_RGB_1210_de28ebb9ea41"
  LinkPlacement = pos=(247.3,-93,0) rot=(0,0,1;0rad)
  LinkedObject = -> Shape
  Placement = pos=(247.3,-93,0) rot=(0,0,1;0rad)
FEATURE [App::Link] D136_LED_RGB_1210_62a520bec992_ln_162  label="D243_LED_RGB_1210_078594ccc235"
  LinkPlacement = pos=(259,-87.4,0) rot=(0,0,1;0rad)
  LinkedObject = -> Shape
  Placement = pos=(259,-87.4,0) rot=(0,0,1;0rad)
FEATURE [App::Link] D136_LED_RGB_1210_62a520bec992_ln_163  label="D91_LED_RGB_1210_8756aca01a02"
  LinkPlacement = pos=(217.9,-124.6,0) rot=(0,0,1;0rad)
  LinkedObject = -> Shape
  Placement = pos=(217.9,-124.6,0) rot=(0,0,1;0rad)
FEATURE [App::Link] D136_LED_RGB_1210_62a520bec992_ln_164  label="D148_LED_RGB_1210_68d30916b9ba"
  LinkPlacement = pos=(185.5,-67,0) rot=(0,0,1;0rad)
  LinkedObject = -> Shape
  Placement = pos=(185.5,-67,0) rot=(0,0,1;0rad)
FEATURE [App::Link] D136_LED_RGB_1210_62a520bec992_ln_165  label="D17_LED_RGB_1210_3426b52f1a59"
  LinkPlacement = pos=(209.55,-162.45,0) rot=(0,0,1;0rad)
  LinkedObject = -> Shape
  Placement = pos=(209.55,-162.45,0) rot=(0,0,1;0rad)
FEATURE [App::Link] D136_LED_RGB_1210_62a520bec992_ln_166  label="D205_LED_RGB_1210_d15f926dc801"
  LinkPlacement = pos=(300.1,-38.2,0) rot=(0,0,1;0rad)
  LinkedObject = -> Shape
  Placement = pos=(300.1,-38.2,0) rot=(0,0,1;0rad)
FEATURE [App::Link] D136_LED_RGB_1210_62a520bec992_ln_167  label="D25_LED_RGB_1210_9bd98ddf9d81"
  LinkPlacement = pos=(177.659,-156.526,0) rot=(0,0,1;0rad)
  LinkedObject = -> Shape
  Placement = pos=(177.659,-156.526,0) rot=(0,0,1;0rad)
FEATURE [App::Link] D136_LED_RGB_1210_62a520bec992_ln_168  label="D204_LED_RGB_1210_2463b917510b"
  LinkPlacement = pos=(290.059,-34.1264,0) rot=(0,0,1;0rad)
  LinkedObject = -> Shape
  Placement = pos=(290.059,-34.1264,0) rot=(0,0,1;0rad)
FEATURE [App::Link] D136_LED_RGB_1210_62a520bec992_ln_170  label="D185_LED_RGB_1210_727e4e3dcfc2"
  LinkPlacement = pos=(269.259,-3.02639,0) rot=(0,0,1;0rad)
  LinkedObject = -> Shape
  Placement = pos=(269.259,-3.02639,0) rot=(0,0,1;0rad)
FEATURE [App::Link] D136_LED_RGB_1210_62a520bec992_ln_171  label="D92_LED_RGB_1210_cbe8e7409ee7"
  LinkPlacement = pos=(224.75,-127.65,0) rot=(0,0,1;0rad)
  LinkedObject = -> Shape
  Placement = pos=(224.75,-127.65,0) rot=(0,0,1;0rad)
FEATURE [App::Link] D136_LED_RGB_1210_62a520bec992_ln_172  label="D183_LED_RGB_1210_df48ac0dd11f"
  LinkPlacement = pos=(263.359,-8.42639,0) rot=(0,0,1;0rad)
  LinkedObject = -> Shape
  Placement = pos=(263.359,-8.42639,0) rot=(0,0,1;0rad)
FEATURE [App::Link] D136_LED_RGB_1210_62a520bec992_ln_173  label="D177_LED_RGB_1210_7b1c4ea80cca"
  LinkPlacement = pos=(243.1,-8.5,0) rot=(0,0,1;0rad)
  LinkedObject = -> Shape
  Placement = pos=(243.1,-8.5,0) rot=(0,0,1;0rad)
FEATURE [App::Link] D136_LED_RGB_1210_62a520bec992_ln_174  label="D230_LED_RGB_1210_bbe5f36ca49a"
  LinkPlacement = pos=(218.459,-44.8264,0) rot=(0,0,1;0rad)
  LinkedObject = -> Shape
  Placement = pos=(218.459,-44.8264,0) rot=(0,0,1;0rad)
FEATURE [App::Link] D136_LED_RGB_1210_62a520bec992_ln_175  label="D20_LED_RGB_1210_448f54947c68"
  LinkPlacement = pos=(198.2,-170.9,0) rot=(0,0,1;0rad)
  LinkedObject = -> Shape
  Placement = pos=(198.2,-170.9,0) rot=(0,0,1;0rad)
FEATURE [App::Link] D136_LED_RGB_1210_62a520bec992_ln_176  label="D142_LED_RGB_1210_d6bca7bfb8b0"
  LinkPlacement = pos=(207.8,-68.65,0) rot=(0,0,1;0rad)
  LinkedObject = -> Shape
  Placement = pos=(207.8,-68.65,0) rot=(0,0,1;0rad)
FEATURE [Part::Feature] Shape005  label="J1_PinHeader_2x04_P127mm_Vertical_bbcf534692e7"
  Placement = pos=(195.6,-106.9,0) rot=(0,0,1;0rad)
  shape: bbox 3.4 x 5.08 x 6.3 mm, 172 faces (baked)
FEATURE [App::Link] D136_LED_RGB_1210_62a520bec992_ln_177  label="D192_LED_RGB_1210_7ea927849d21"
  LinkPlacement = pos=(311,-8.5,0) rot=(0,0,1;0rad)
  LinkedObject = -> Shape
  Placement = pos=(311,-8.5,0) rot=(0,0,1;0rad)
FEATURE [App::Link] D136_LED_RGB_1210_62a520bec992_ln_178  label="D209_LED_RGB_1210_4e222f9b7870"
  LinkPlacement = pos=(293.659,-44.7264,0) rot=(0,0,1;0rad)
  LinkedObject = -> Shape
  Placement = pos=(293.659,-44.7264,0) rot=(0,0,1;0rad)
FEATURE [App::Link] D136_LED_RGB_1210_62a520bec992_ln_179  label="D70_LED_RGB_1210_a467c5f30b70"
  LinkPlacement = pos=(254.15,-154.45,0) rot=(0,0,1;0rad)
  LinkedObject = -> Shape
  Placement = pos=(254.15,-154.45,0) rot=(0,0,1;0rad)
FEATURE [App::Link] D136_LED_RGB_1210_62a520bec992_ln_180  label="D163_LED_RGB_1210_75e9770f6cb7"
  LinkPlacement = pos=(208.9,-42.5,0) rot=(0,0,1;0rad)
  LinkedObject = -> Shape
  Placement = pos=(208.9,-42.5,0) rot=(0,0,1;0rad)
FEATURE [App::Link] C2_C_1206_3216Metric_b79cb4619a35_ln_003  label="C41_C_1206_3216Metric_20f47943d814"
  LinkPlacement = pos=(231.8,-129.5,0) rot=(0,0,1;0rad)
  LinkedObject = -> Shape002
  Placement = pos=(231.8,-129.5,0) rot=(0,0,1;0rad)
FEATURE [App::Link] D136_LED_RGB_1210_62a520bec992_ln_182  label="D225_LED_RGB_1210_09671b005a60"
  LinkPlacement = pos=(241.9,-54.1,0) rot=(0,0,1;0rad)
  LinkedObject = -> Shape
  Placement = pos=(241.9,-54.1,0) rot=(0,0,1;0rad)
FEATURE [App::Link] D136_LED_RGB_1210_62a520bec992_ln_183  label="D83_LED_RGB_1210_84f9544fae19"
  LinkPlacement = pos=(229.259,-185.026,0) rot=(0,0,1;0rad)
  LinkedObject = -> Shape
  Placement = pos=(229.259,-185.026,0) rot=(0,0,1;0rad)
FEATURE [App::Link] D136_LED_RGB_1210_62a520bec992_ln_184  label="D202_LED_RGB_1210_48ab6d9b57b5"
  LinkPlacement = pos=(300.059,-33.5264,0) rot=(0,0,1;0rad)
  LinkedObject = -> Shape
  Placement = pos=(300.059,-33.5264,0) rot=(0,0,1;0rad)
FEATURE [App::Link] D136_LED_RGB_1210_62a520bec992_ln_185  label="D112_LED_RGB_1210_742dc8964f07"
  LinkPlacement = pos=(265.359,-111.126,0) rot=(0,0,1;0rad)
  LinkedObject = -> Shape
  Placement = pos=(265.359,-111.126,0) rot=(0,0,1;0rad)
FEATURE [App::Link] D136_LED_RGB_1210_62a520bec992_ln_186  label="D240_LED_RGB_1210_becd10057cf7"
  LinkPlacement = pos=(246.559,-83.9264,0) rot=(0,0,1;0rad)
  LinkedObject = -> Shape
  Placement = pos=(246.559,-83.9264,0) rot=(0,0,1;0rad)
FEATURE [App::Link] D136_LED_RGB_1210_62a520bec992_ln_187  label="D244_LED_RGB_1210_4dc3f7d05774"
  LinkPlacement = pos=(260.659,-83.1264,0) rot=(0,0,1;0rad)
  LinkedObject = -> Shape
  Placement = pos=(260.659,-83.1264,0) rot=(0,0,1;0rad)
FEATURE [App::Link] D136_LED_RGB_1210_62a520bec992_ln_188  label="D61_LED_RGB_1210_130ad883e12b"
  LinkPlacement = pos=(266.259,-178.626,0) rot=(0,0,1;0rad)
  LinkedObject = -> Shape
  Placement = pos=(266.259,-178.626,0) rot=(0,0,1;0rad)
FEATURE [App::Link] D136_LED_RGB_1210_62a520bec992_ln_189  label="D241_LED_RGB_1210_43b5cb1b6f47"
  LinkPlacement = pos=(252.159,-87.7264,0) rot=(0,0,1;0rad)
  LinkedObject = -> Shape
  Placement = pos=(252.159,-87.7264,0) rot=(0,0,1;0rad)
FEATURE [App::Link] D136_LED_RGB_1210_62a520bec992_ln_190  label="D1_LED_RGB_1210_6b028d333a99"
  LinkPlacement = pos=(172.059,-117.226,0) rot=(0,0,1;0rad)
  LinkedObject = -> Shape
  Placement = pos=(172.059,-117.226,0) rot=(0,0,1;0rad)
FEATURE [App::Link] C2_C_1206_3216Metric_b79cb4619a35_ln_004  label="C38_C_1206_3216Metric_d1ed8c57e6f8"
  LinkPlacement = pos=(220.457,-173.757,0) rot=(0,0,1;2.35619rad)
  LinkedObject = -> Shape002
  Placement = pos=(220.457,-173.757,0) rot=(0,0,1;2.35619rad)
FEATURE [App::Link] D136_LED_RGB_1210_62a520bec992_ln_191  label="D126_LED_RGB_1210_7d406970ee79"
  LinkPlacement = pos=(198.45,-93.95,0) rot=(0,0,1;0rad)
  LinkedObject = -> Shape
  Placement = pos=(198.45,-93.95,0) rot=(0,0,1;0rad)
FEATURE [App::Link] D136_LED_RGB_1210_62a520bec992_ln_192  label="D124_LED_RGB_1210_f4968298951b"
  LinkPlacement = pos=(207.359,-87.8264,0) rot=(0,0,1;0rad)
  LinkedObject = -> Shape
  Placement = pos=(207.359,-87.8264,0) rot=(0,0,1;0rad)
FEATURE [App::Link] D136_LED_RGB_1210_62a520bec992_ln_193  label="D27_LED_RGB_1210_ca9e65bc3320"
  LinkPlacement = pos=(182.059,-150.026,0) rot=(0,0,1;0rad)
  LinkedObject = -> Shape
  Placement = pos=(182.059,-150.026,0) rot=(0,0,1;0rad)
FEATURE [App::Link] D136_LED_RGB_1210_62a520bec992_ln_194  label="D161_LED_RGB_1210_09d76a1110d8"
  LinkPlacement = pos=(197.259,-42.2264,0) rot=(0,0,1;0rad)
  LinkedObject = -> Shape
  Placement = pos=(197.259,-42.2264,0) rot=(0,0,1;0rad)
FEATURE [App::Link] D136_LED_RGB_1210_62a520bec992_ln_195  label="D6_LED_RGB_1210_19731e050e85"
  LinkPlacement = pos=(177.659,-128.426,0) rot=(0,0,1;0rad)
  LinkedObject = -> Shape
  Placement = pos=(177.659,-128.426,0) rot=(0,0,1;0rad)
FEATURE [App::Link] D136_LED_RGB_1210_62a520bec992_ln_196  label="D118_LED_RGB_1210_cf94cf054be3"
  LinkPlacement = pos=(230.55,-87.15,0) rot=(0,0,1;0rad)
  LinkedObject = -> Shape
  Placement = pos=(230.55,-87.15,0) rot=(0,0,1;0rad)
FEATURE [App::Link] D136_LED_RGB_1210_62a520bec992_ln_197  label="D159_LED_RGB_1210_bec7924a42f0"
  LinkPlacement = pos=(193.7,-47.9,0) rot=(0,0,1;0rad)
  LinkedObject = -> Shape
  Placement = pos=(193.7,-47.9,0) rot=(0,0,1;0rad)
FEATURE [App::Link] D136_LED_RGB_1210_62a520bec992_ln_198  label="D224_LED_RGB_1210_890333756dbf"
  LinkPlacement = pos=(248.4,-53.1,0) rot=(0,0,1;0rad)
  LinkedObject = -> Shape
  Placement = pos=(248.4,-53.1,0) rot=(0,0,1;0rad)
FEATURE [App::Link] D136_LED_RGB_1210_62a520bec992_ln_199  label="D160_LED_RGB_1210_fc49052343ca"
  LinkPlacement = pos=(200.859,-46.1264,0) rot=(0,0,1;0rad)
  LinkedObject = -> Shape
  Placement = pos=(200.859,-46.1264,0) rot=(0,0,1;0rad)
FEATURE [App::Link] D136_LED_RGB_1210_62a520bec992_ln_200  label="D80_LED_RGB_1210_dda1010e7a67"
  LinkPlacement = pos=(224.65,-169.95,0) rot=(0,0,1;0rad)
  LinkedObject = -> Shape
  Placement = pos=(224.65,-169.95,0) rot=(0,0,1;0rad)
FEATURE [App::Link] D136_LED_RGB_1210_62a520bec992_ln_201  label="D65_LED_RGB_1210_df06d4cd79c9"
  LinkPlacement = pos=(262.25,-166.55,0) rot=(0,0,1;0rad)
  LinkedObject = -> Shape
  Placement = pos=(262.25,-166.55,0) rot=(0,0,1;0rad)
FEATURE [App::Link] D136_LED_RGB_1210_62a520bec992_ln_202  label="D228_LED_RGB_1210_dd3448906e70"
  LinkPlacement = pos=(225.359,-50.5264,0) rot=(0,0,1;0rad)
  LinkedObject = -> Shape
  Placement = pos=(225.359,-50.5264,0) rot=(0,0,1;0rad)
FEATURE [App::Link] D136_LED_RGB_1210_62a520bec992_ln_203  label="D97_LED_RGB_1210_777273cc3965"
  LinkPlacement = pos=(235.9,-133.5,0) rot=(0,0,1;0rad)
  LinkedObject = -> Shape
  Placement = pos=(235.9,-133.5,0) rot=(0,0,1;0rad)
FEATURE [App::Link] D136_LED_RGB_1210_62a520bec992_ln_204  label="D135_LED_RGB_1210_b6299023a874"
  LinkPlacement = pos=(195.559,-102.526,0) rot=(0,0,1;0rad)
  LinkedObject = -> Shape
  Placement = pos=(195.559,-102.526,0) rot=(0,0,1;0rad)
FEATURE [App::Link] D136_LED_RGB_1210_62a520bec992_ln_205  label="D74_LED_RGB_1210_ad6a4d967366"
  LinkPlacement = pos=(234.7,-154.1,0) rot=(0,0,1;0rad)
  LinkedObject = -> Shape
  Placement = pos=(234.7,-154.1,0) rot=(0,0,1;0rad)
FEATURE [App::Link] D136_LED_RGB_1210_62a520bec992_ln_206  label="D73_LED_RGB_1210_81896658d542"
  LinkPlacement = pos=(239.4,-155.2,0) rot=(0,0,1;0rad)
  LinkedObject = -> Shape
  Placement = pos=(239.4,-155.2,0) rot=(0,0,1;0rad)
FEATURE [Part::Feature] Shape006  label="J14_R_Axial_DIN0207_L63mm_D25mm_P1016mm_Horizontal_16070ee27b5d"
  Placement = pos=(176.85,-146.475,0) rot=(0,0,1;1.5708rad)
  shape: bbox 2.706 x 10.96 x 5.603 mm, 17 faces (baked)
FEATURE [App::Link] D136_LED_RGB_1210_62a520bec992_ln_207  label="D201_LED_RGB_1210_79ee7934fa27"
  LinkPlacement = pos=(294.059,-26.9264,0) rot=(0,0,1;0rad)
  LinkedObject = -> Shape
  Placement = pos=(294.059,-26.9264,0) rot=(0,0,1;0rad)
FEATURE [App::Link] D136_LED_RGB_1210_62a520bec992_ln_208  label="D179_LED_RGB_1210_059795b28a81"
  LinkPlacement = pos=(248.259,-5.82639,0) rot=(0,0,1;0rad)
  LinkedObject = -> Shape
  Placement = pos=(248.259,-5.82639,0) rot=(0,0,1;0rad)
FEATURE [Part::Feature] Shape007  label="C1_C_0402_1005Metric_dadc7bec6630"
  Placement = pos=(279,-72.9,0) rot=(0,0,-1;1.5708rad)
  shape: bbox 0.5 x 1 x 0.5 mm, 28 faces (baked)
FEATURE [App::Link] D136_LED_RGB_1210_62a520bec992_ln_209  label="D26_LED_RGB_1210_d322e4015a61"
  LinkPlacement = pos=(176,-151.7,0) rot=(0,0,1;0rad)
  LinkedObject = -> Shape
  Placement = pos=(176,-151.7,0) rot=(0,0,1;0rad)
FEATURE [App::Link] D136_LED_RGB_1210_62a520bec992_ln_210  label="D102_LED_RGB_1210_78c733efda66"
  LinkPlacement = pos=(260.7,-151.3,0) rot=(0,0,1;0rad)
  LinkedObject = -> Shape
  Placement = pos=(260.7,-151.3,0) rot=(0,0,1;0rad)
FEATURE [App::Link] D136_LED_RGB_1210_62a520bec992_ln_211  label="D199_LED_RGB_1210_fcb8b2203b1a"
  LinkPlacement = pos=(297.159,-22.6264,0) rot=(0,0,1;0rad)
  LinkedObject = -> Shape
  Placement = pos=(297.159,-22.6264,0) rot=(0,0,1;0rad)
FEATURE [App::Link] D136_LED_RGB_1210_62a520bec992_ln_212  label="D217_LED_RGB_1210_31da4e75d9e5"
  LinkPlacement = pos=(280.3,-58.55,0) rot=(0,0,1;0rad)
  LinkedObject = -> Shape
  Placement = pos=(280.3,-58.55,0) rot=(0,0,1;0rad)
FEATURE [App::Link] D136_LED_RGB_1210_62a520bec992_ln_213  label="D203_LED_RGB_1210_fe8c48dbb5c8"
  LinkPlacement = pos=(294.859,-31.2264,0) rot=(0,0,1;0rad)
  LinkedObject = -> Shape
  Placement = pos=(294.859,-31.2264,0) rot=(0,0,1;0rad)
FEATURE [App::Link] D136_LED_RGB_1210_62a520bec992_ln_214  label="D127_LED_RGB_1210_621b6d9ce413"
  LinkPlacement = pos=(196.2,-97.9,0) rot=(0,0,1;0rad)
  LinkedObject = -> Shape
  Placement = pos=(196.2,-97.9,0) rot=(0,0,1;0rad)
FEATURE [App::Link] D136_LED_RGB_1210_62a520bec992_ln_215  label="D166_LED_RGB_1210_56c0e81d4a94"
  LinkPlacement = pos=(207.559,-32.8264,0) rot=(0,0,1;0rad)
  LinkedObject = -> Shape
  Placement = pos=(207.559,-32.8264,0) rot=(0,0,1;0rad)
FEATURE [App::Link] D136_LED_RGB_1210_62a520bec992_ln_216  label="D119_LED_RGB_1210_ae58d8b93f91"
  LinkPlacement = pos=(224.9,-84.6,0) rot=(0,0,1;0rad)
  LinkedObject = -> Shape
  Placement = pos=(224.9,-84.6,0) rot=(0,0,1;0rad)
FEATURE [App::Link] D136_LED_RGB_1210_62a520bec992_ln_217  label="D245_LED_RGB_1210_37488ec00b28"
  LinkPlacement = pos=(263.9,-86.4,0) rot=(0,0,1;0rad)
  LinkedObject = -> Shape
  Placement = pos=(263.9,-86.4,0) rot=(0,0,1;0rad)
FEATURE [App::Link] D136_LED_RGB_1210_62a520bec992_ln_218  label="D236_LED_RGB_1210_fd3f10fe8ed8"
  LinkPlacement = pos=(234.8,-84.3,0) rot=(0,0,1;0rad)
  LinkedObject = -> Shape
  Placement = pos=(234.8,-84.3,0) rot=(0,0,1;0rad)
FEATURE [App::Link] D136_LED_RGB_1210_62a520bec992_ln_219  label="D4_LED_RGB_1210_1d2686d34f67"
  LinkPlacement = pos=(171.759,-126.426,0) rot=(0,0,1;0rad)
  LinkedObject = -> Shape
  Placement = pos=(171.759,-126.426,0) rot=(0,0,1;0rad)
FEATURE [App::Link] D136_LED_RGB_1210_62a520bec992_ln_221  label="D173_LED_RGB_1210_6b8953eacd5e"
  LinkPlacement = pos=(231.4,-20.15,0) rot=(0,0,1;0rad)
  LinkedObject = -> Shape
  Placement = pos=(231.4,-20.15,0) rot=(0,0,1;0rad)
FEATURE [App::Link] D136_LED_RGB_1210_62a520bec992_ln_222  label="D188_LED_RGB_1210_b59e2be4193b"
  LinkPlacement = pos=(297.159,-10.1264,0) rot=(0,0,1;0rad)
  LinkedObject = -> Shape
  Placement = pos=(297.159,-10.1264,0) rot=(0,0,1;0rad)
FEATURE [App::Link] D136_LED_RGB_1210_62a520bec992_ln_223  label="D208_LED_RGB_1210_05e4ea57a827"
  LinkPlacement = pos=(289.2,-39.3,0) rot=(0,0,1;0rad)
  LinkedObject = -> Shape
  Placement = pos=(289.2,-39.3,0) rot=(0,0,1;0rad)
FEATURE [App::Link] D136_LED_RGB_1210_62a520bec992_ln_224  label="D211_LED_RGB_1210_b65aebb00048"
  LinkPlacement = pos=(288.459,-49.3264,0) rot=(0,0,1;0rad)
  LinkedObject = -> Shape
  Placement = pos=(288.459,-49.3264,0) rot=(0,0,1;0rad)
FEATURE [App::Link] D136_LED_RGB_1210_62a520bec992_ln_225  label="D66_LED_RGB_1210_bfe3aef8addf"
  LinkPlacement = pos=(258.15,-164.05,0) rot=(0,0,1;0rad)
  LinkedObject = -> Shape
  Placement = pos=(258.15,-164.05,0) rot=(0,0,1;0rad)
FEATURE [App::Link] D136_LED_RGB_1210_62a520bec992_ln_227  label="D128_LED_RGB_1210_09d92648d208"
  LinkPlacement = pos=(191.5,-96.4,0) rot=(0,0,1;0rad)
  LinkedObject = -> Shape
  Placement = pos=(191.5,-96.4,0) rot=(0,0,1;0rad)
FEATURE [App::Link] D136_LED_RGB_1210_62a520bec992_ln_228  label="D200_LED_RGB_1210_a49b83244f6f"
  LinkPlacement = pos=(299.559,-29.0264,0) rot=(0,0,1;0rad)
  LinkedObject = -> Shape
  Placement = pos=(299.559,-29.0264,0) rot=(0,0,1;0rad)
FEATURE [App::Link] D136_LED_RGB_1210_62a520bec992_ln_229  label="D234_LED_RGB_1210_26dbe84589c0"
  LinkPlacement = pos=(221.5,-66.6,0) rot=(0,0,1;0rad)
  LinkedObject = -> Shape
  Placement = pos=(221.5,-66.6,0) rot=(0,0,1;0rad)
FEATURE [App::Link] D136_LED_RGB_1210_62a520bec992_ln_230  label="D77_LED_RGB_1210_20c7d5b6ff53"
  LinkPlacement = pos=(223.059,-152.626,0) rot=(0,0,1;0rad)
  LinkedObject = -> Shape
  Placement = pos=(223.059,-152.626,0) rot=(0,0,1;0rad)
FEATURE [App::Link] D136_LED_RGB_1210_62a520bec992_ln_231  label="D116_LED_RGB_1210_f767cc3f7f36"
  LinkPlacement = pos=(251.65,-96.15,0) rot=(0,0,1;0rad)
  LinkedObject = -> Shape
  Placement = pos=(251.65,-96.15,0) rot=(0,0,1;0rad)
FEATURE [App::Link] D136_LED_RGB_1210_62a520bec992_ln_232  label="D37_LED_RGB_1210_e2949ee7ab56"
  LinkPlacement = pos=(203.659,-195.526,0) rot=(0,0,1;0rad)
  LinkedObject = -> Shape
  Placement = pos=(203.659,-195.526,0) rot=(0,0,1;0rad)
FEATURE [App::Link] D136_LED_RGB_1210_62a520bec992_ln_233  label="D125_LED_RGB_1210_a3e2201ea1ff"
  LinkPlacement = pos=(203.8,-91.8,0) rot=(0,0,1;0rad)
  LinkedObject = -> Shape
  Placement = pos=(203.8,-91.8,0) rot=(0,0,1;0rad)
FEATURE [App::Link] D136_LED_RGB_1210_62a520bec992_ln_234  label="D233_LED_RGB_1210_16cf2f89d60c"
  LinkPlacement = pos=(223.3,-61.5,0) rot=(0,0,1;0rad)
  LinkedObject = -> Shape
  Placement = pos=(223.3,-61.5,0) rot=(0,0,1;0rad)
FEATURE [App::Link] D136_LED_RGB_1210_62a520bec992_ln_235  label="D242_LED_RGB_1210_78fcb7bc90a9"
  LinkPlacement = pos=(254.359,-83.7264,0) rot=(0,0,1;0rad)
  LinkedObject = -> Shape
  Placement = pos=(254.359,-83.7264,0) rot=(0,0,1;0rad)
FEATURE [App::Link] D136_LED_RGB_1210_62a520bec992_ln_236  label="D76_LED_RGB_1210_eb4e5e9360d1"
  LinkPlacement = pos=(229,-153.6,0) rot=(0,0,1;0rad)
  LinkedObject = -> Shape
  Placement = pos=(229,-153.6,0) rot=(0,0,1;0rad)
FEATURE [App::Link] D136_LED_RGB_1210_62a520bec992_ln_237  label="D5_LED_RGB_1210_38a768f6ff60"
  LinkPlacement = pos=(171.959,-131.126,0) rot=(0,0,1;0rad)
  LinkedObject = -> Shape
  Placement = pos=(171.959,-131.126,0) rot=(0,0,1;0rad)
FEATURE [App::Link] D136_LED_RGB_1210_62a520bec992_ln_238  label="D110_LED_RGB_1210_acdd5e2feb0e"
  LinkPlacement = pos=(264.4,-120.9,0) rot=(0,0,1;0rad)
  LinkedObject = -> Shape
  Placement = pos=(264.4,-120.9,0) rot=(0,0,1;0rad)
FEATURE [App::Link] D136_LED_RGB_1210_62a520bec992_ln_239  label="D157_LED_RGB_1210_c0e06cd55aba"
  LinkPlacement = pos=(190.1,-53.7,0) rot=(0,0,1;0rad)
  LinkedObject = -> Shape
  Placement = pos=(190.1,-53.7,0) rot=(0,0,1;0rad)
FEATURE [App::Link] D136_LED_RGB_1210_62a520bec992_ln_240  label="D139_LED_RGB_1210_db306bf74fe4"
  LinkPlacement = pos=(208.2,-78.9,0) rot=(0,0,1;0rad)
  LinkedObject = -> Shape
  Placement = pos=(208.2,-78.9,0) rot=(0,0,1;0rad)
FEATURE [App::Link] D136_LED_RGB_1210_62a520bec992_ln_241  label="D237_LED_RGB_1210_65dd3d4be95c"
  LinkPlacement = pos=(238.059,-89.3264,0) rot=(0,0,1;0rad)
  LinkedObject = -> Shape
  Placement = pos=(238.059,-89.3264,0) rot=(0,0,1;0rad)
FEATURE [App::Link] D136_LED_RGB_1210_62a520bec992_ln_242  label="D140_LED_RGB_1210_bfcbfa088295"
  LinkPlacement = pos=(214.3,-78,0) rot=(0,0,1;0rad)
  LinkedObject = -> Shape
  Placement = pos=(214.3,-78,0) rot=(0,0,1;0rad)
FEATURE [App::Link] D136_LED_RGB_1210_62a520bec992_ln_243  label="D152_LED_RGB_1210_2798b454a660"
  LinkPlacement = pos=(178,-83.4,0) rot=(0,0,1;0rad)
  LinkedObject = -> Shape
  Placement = pos=(178,-83.4,0) rot=(0,0,1;0rad)
FEATURE [App::Link] D136_LED_RGB_1210_62a520bec992_ln_244  label="D43_LED_RGB_1210_fd0b56c9018b"
  LinkPlacement = pos=(228.6,-195.2,0) rot=(0,0,1;0rad)
  LinkedObject = -> Shape
  Placement = pos=(228.6,-195.2,0) rot=(0,0,1;0rad)
FEATURE [App::Link] D136_LED_RGB_1210_62a520bec992_ln_245  label="D99_LED_RGB_1210_7160f6f0e956"
  LinkPlacement = pos=(245.859,-141.426,0) rot=(0,0,1;0rad)
  LinkedObject = -> Shape
  Placement = pos=(245.859,-141.426,0) rot=(0,0,1;0rad)
FEATURE [App::Link] D136_LED_RGB_1210_62a520bec992_ln_246  label="D169_LED_RGB_1210_775aa17d46a3"
  LinkPlacement = pos=(217.559,-28.7264,0) rot=(0,0,1;0rad)
  LinkedObject = -> Shape
  Placement = pos=(217.559,-28.7264,0) rot=(0,0,1;0rad)
FEATURE [App::Link] D136_LED_RGB_1210_62a520bec992_ln_247  label="D171_LED_RGB_1210_29afbe46dcc2"
  LinkPlacement = pos=(223.55,-24.45,0) rot=(0,0,1;0rad)
  LinkedObject = -> Shape
  Placement = pos=(223.55,-24.45,0) rot=(0,0,1;0rad)
FEATURE [App::Link] D136_LED_RGB_1210_62a520bec992_ln_248  label="D195_LED_RGB_1210_c7b63fb3344d"
  LinkPlacement = pos=(304.3,-15.9,0) rot=(0,0,1;0rad)
  LinkedObject = -> Shape
  Placement = pos=(304.3,-15.9,0) rot=(0,0,1;0rad)
FEATURE [App::Link] D136_LED_RGB_1210_62a520bec992_ln_249  label="D235_LED_RGB_1210_11724cadf89a"
  LinkPlacement = pos=(218.35,-72.55,0) rot=(0,0,1;0rad)
  LinkedObject = -> Shape
  Placement = pos=(218.35,-72.55,0) rot=(0,0,1;0rad)
FEATURE [App::Link] D136_LED_RGB_1210_62a520bec992_ln_250  label="D130_LED_RGB_1210_f7cbcefeb4fb"
  LinkPlacement = pos=(177.759,-115.326,0) rot=(0,0,1;0rad)
  LinkedObject = -> Shape
  Placement = pos=(177.759,-115.326,0) rot=(0,0,1;0rad)
FEATURE [App::Link] D136_LED_RGB_1210_62a520bec992_ln_252  label="D151_LED_RGB_1210_627f613ba0c9"
  LinkPlacement = pos=(176.7,-78.8,0) rot=(0,0,1;0rad)
  LinkedObject = -> Shape
  Placement = pos=(176.7,-78.8,0) rot=(0,0,1;0rad)
FEATURE [App::Link] D136_LED_RGB_1210_62a520bec992_ln_253  label="D168_LED_RGB_1210_38409df31661"
  LinkPlacement = pos=(212.15,-27.55,0) rot=(0,0,1;0rad)
  LinkedObject = -> Shape
  Placement = pos=(212.15,-27.55,0) rot=(0,0,1;0rad)
FEATURE [App::Link] D136_LED_RGB_1210_62a520bec992_ln_254  label="D59_LED_RGB_1210_81ad3d4ac7a5"
  LinkPlacement = pos=(267.4,-185.2,0) rot=(0,0,1;0rad)
  LinkedObject = -> Shape
  Placement = pos=(267.4,-185.2,0) rot=(0,0,1;0rad)
FEATURE [App::Part] Top_1785
  Group = -> [Shape,D136_LED_RGB_1210_62a520bec992_ln_,D136_LED_RGB_1210_62a520bec992_ln_001,D136_LED_RGB_1210_62a520bec992_ln_002,D136_LED_RGB_1210_62a520bec992_ln_003,D136_LED_RGB_1210_62a520bec992_ln_004,D136_LED_RGB_1210_62a520bec992_ln_005,D136_LED_RGB_1210_62a520bec992_ln_006,D136_LED_RGB_1210_62a520bec992_ln_007,D136_LED_RGB_1210_62a520bec992_ln_008,D136_LED_RGB_1210_62a520bec992_ln_009,+251 more]
  Origin = -> Origin003
FEATURE [App::Part] Step_Models_1785
  Group = -> [Top_1785]
  Origin = -> Origin002
FEATURE [App::Part] Board_1785  label="StarboardWing"
  Group = -> [Local_CS_1785,Board_Geoms_1785,Step_Models_1785]
  Origin = -> Origin001
